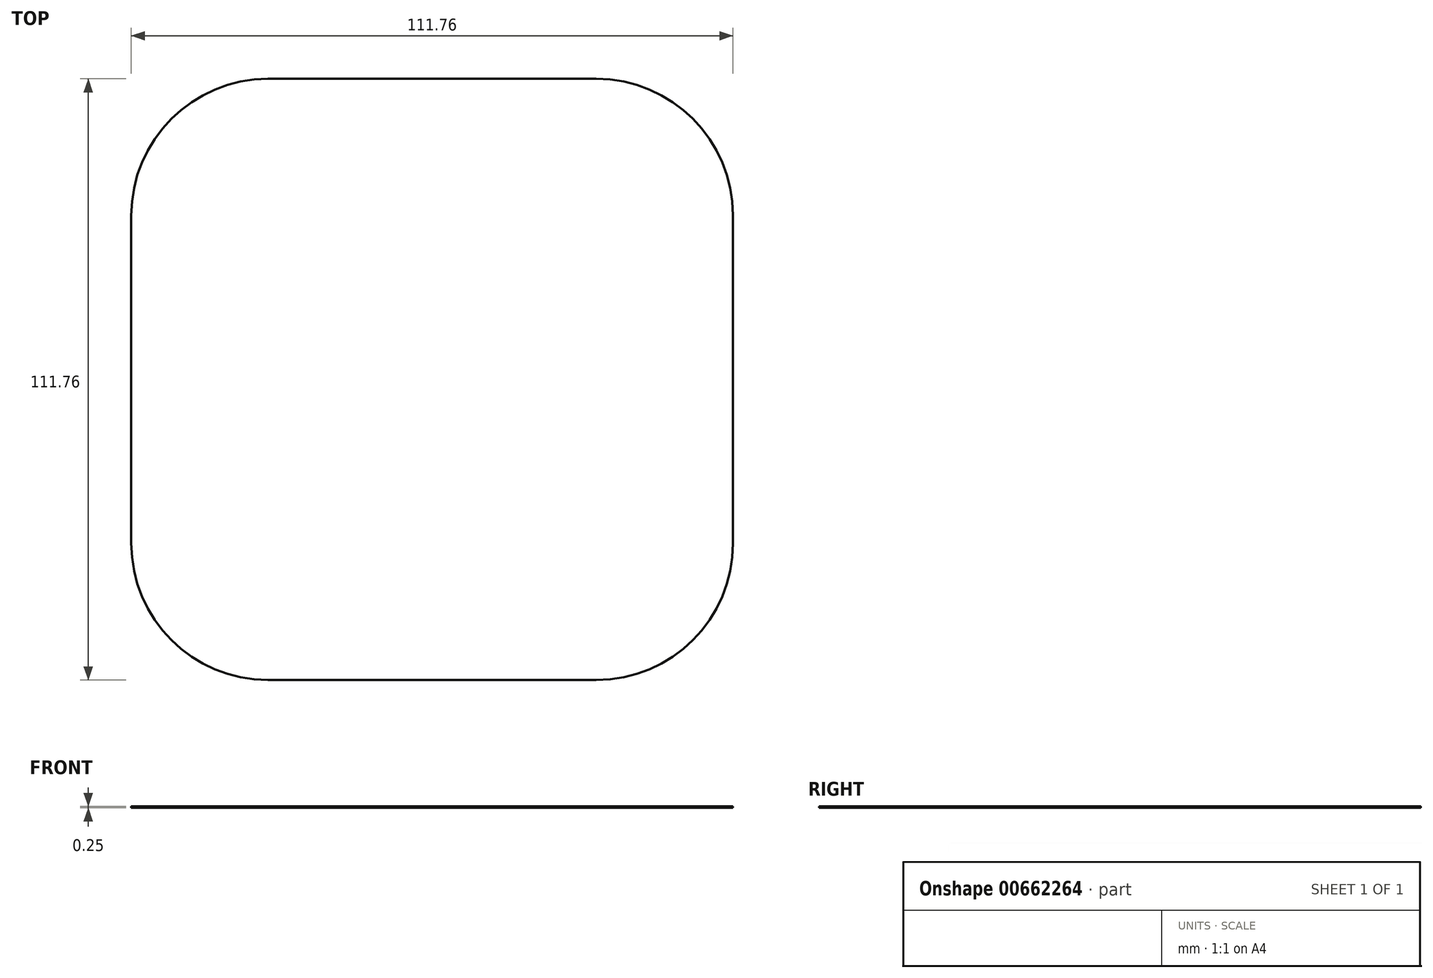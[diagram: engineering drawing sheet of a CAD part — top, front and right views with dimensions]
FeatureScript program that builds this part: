
annotation { "Feature Type Name" : "Feature", "Feature Type Description" : "" }
export const myFeature = defineFeature(function(context is Context, id is Id, definition is map)
    precondition{}
    {
        {
            var Q0;
            Q0=qCreatedBy(makeId("Top.planeOp"),FACE);
            var sketch = newSketch(context, id + "F0", { "sketchPlane" : qUnion([Q0])});
            skPoint(sketch, "E0.middle", {"position": v(0, 0) * mm});
            skLineSegment(sketch, "E1.bottom", {"start": v(30.48, -55.88) * mm, "end": v(-30.48, -55.88) * mm});
            skLineSegment(sketch, "E1.top", {"start": v(30.48, 55.88) * mm, "end": v(-30.48, 55.88) * mm});
            skLineSegment(sketch, "E1.left", {"start": v(55.88, -30.48) * mm, "end": v(55.88, 30.48) * mm});
            skLineSegment(sketch, "E1.right", {"start": v(-55.88, -30.48) * mm, "end": v(-55.88, 30.48) * mm});
            skPoint(sketch, "E2.visualSharp", {"position": v(-55.88, 55.88) * mm});
            skArc(sketch, "E2.filletArc", {"start": v(-30.48, 55.88) * mm, "mid": v(-48.44, 48.44) * mm, "end": v(-55.88, 30.48) * mm});
            skPoint(sketch, "E3.visualSharp", {"position": v(-55.88, -55.88) * mm});
            skArc(sketch, "E3.filletArc", {"start": v(-55.88, -30.48) * mm, "mid": v(-48.44, -48.44) * mm, "end": v(-30.48, -55.88) * mm});
            skArc(sketch, "E4.filletArc", {"start": v(30.48, -55.88) * mm, "mid": v(48.44, -48.44) * mm, "end": v(55.88, -30.48) * mm});
            skArc(sketch, "E5.filletArc", {"start": v(55.88, 30.48) * mm, "mid": v(48.44, 48.44) * mm, "end": v(30.48, 55.88) * mm});
            skSolve(sketch);
        }
        {
            var Q0;
            Q0=qSketchRegion(id+"F0",true);
            extrude(context, id + "F1", {"entities" : qUnion([Q0]), "depth" : 0.25 * mm, "offsetDistance" : 25.4 * mm});
        }
    });
